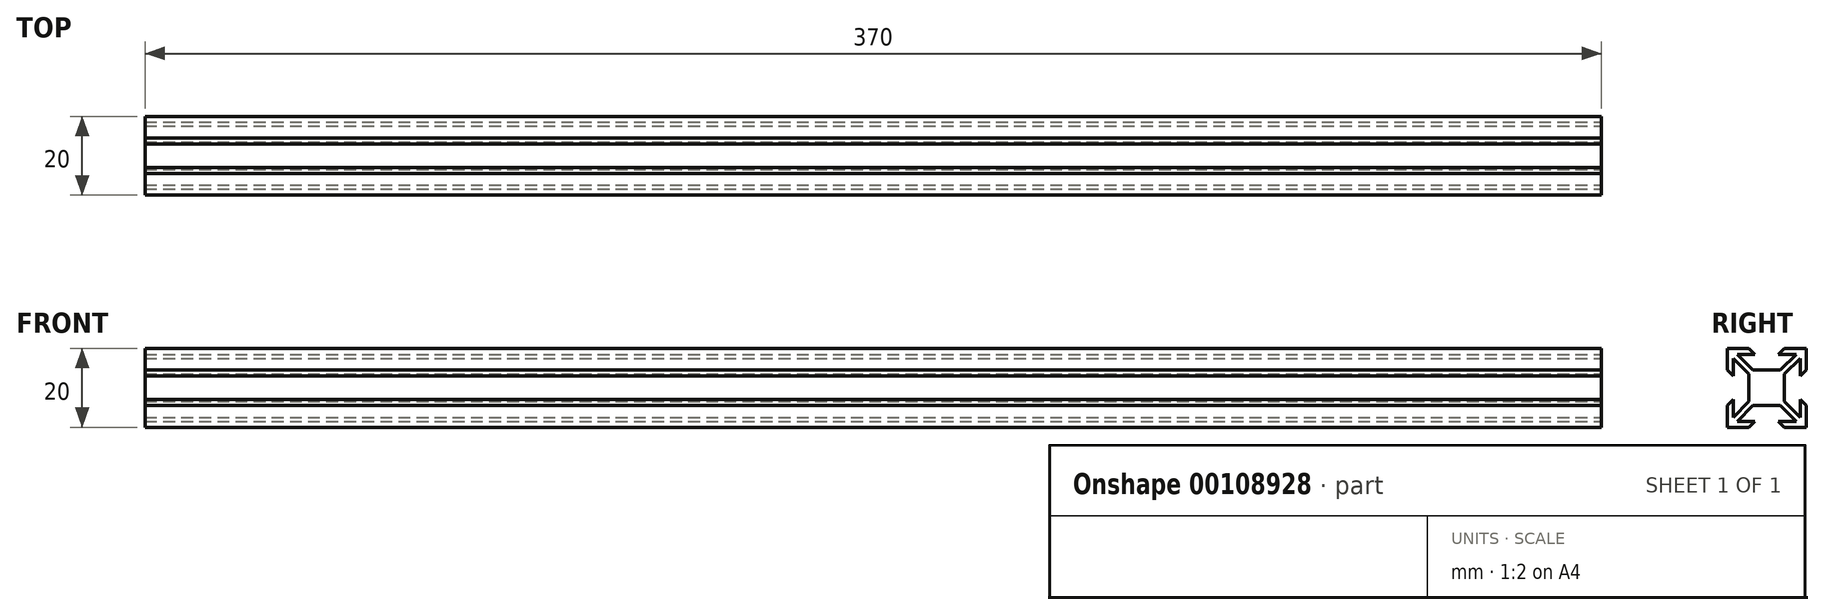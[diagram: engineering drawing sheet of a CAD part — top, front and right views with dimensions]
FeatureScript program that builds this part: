
annotation { "Feature Type Name" : "Feature", "Feature Type Description" : "" }
export const myFeature = defineFeature(function(context is Context, id is Id, definition is map)
    precondition{}
    {
        {
            var Q0;
            Q0=qCreatedBy(makeId("Top.planeOp"),FACE);
            var sketch = newSketch(context, id + "F0", { "sketchPlane" : qUnion([Q0])});
            skLineSegment(sketch, "E0.bottom", {"start": v(-185, 10) * mm, "end": v(185, 10) * mm});
            skLineSegment(sketch, "E0.top", {"start": v(-185, -10) * mm, "end": v(185, -10) * mm});
            skLineSegment(sketch, "E0.left", {"start": v(-185, 10) * mm, "end": v(-185, -10) * mm});
            skLineSegment(sketch, "E0.right", {"start": v(185, 10) * mm, "end": v(185, -10) * mm});
            skPoint(sketch, "E0.middle", {"position": v(0, 0) * mm});
            skSolve(sketch);
        }
        {
            var Q0;
            Q0=makeQuery(id+"F0.imprint","IMPRINT",FACE,{"disambiguationData":[TD([[makeQuery(id+"F0.imprint","IMPRINT",EDGE,{"derivedFrom":sQuery(id+"F0.wireOp",EDGE,"E0.bottom")}),-1.0]])]});
            extrude(context, id + "F1", {"entities" : qUnion([Q0]), "endBound" : BoundingType.SYMMETRIC, "depth" : 20 * mm});
        }
        {
            var Q0;
            Q0=makeQuery(id+"F1.opExtrude","SWEPT_FACE",FACE,{"disambiguationData":[OSD([sQuery(id+"F0.wireOp",EDGE,"E0.right")])]});
            var sketch = newSketch(context, id + "F2", { "sketchPlane" : qUnion([Q0])});
            skLineSegment(sketch, "E1", {"start": v(-4.5, 10) * mm, "end": v(-3, 8.5) * mm});
            skLineSegment(sketch, "E2", {"start": v(-3, 8.5) * mm, "end": v(-7.5, 8.5) * mm});
            skLineSegment(sketch, "E3", {"start": v(-7.5, 8.5) * mm, "end": v(-3.5, 4.5) * mm});
            skLineSegment(sketch, "E4", {"start": v(-3.5, 4.5) * mm, "end": v(0, 4.5) * mm});
            skLineSegment(sketch, "E5", {"start": v(0, 10) * mm, "end": v(0, -10) * mm, "construction": true});
            skLineSegment(sketch, "E6", {"start": v(-10, 0) * mm, "end": v(10, 0) * mm, "construction": true});
            skLineSegment(sketch, "E7.MirrorCS", {"start": v(-3.5, -4.5) * mm, "end": v(0, -4.5) * mm});
            skLineSegment(sketch, "E8.MirrorCS", {"start": v(-7.5, -8.5) * mm, "end": v(-3.5, -4.5) * mm});
            skLineSegment(sketch, "E9.MirrorCS", {"start": v(-3, -8.5) * mm, "end": v(-7.5, -8.5) * mm});
            skLineSegment(sketch, "E10.MirrorCS", {"start": v(-4.5, -10) * mm, "end": v(-3, -8.5) * mm});
            skLineSegment(sketch, "E11.MirrorCS", {"start": v(4.5, 10) * mm, "end": v(3, 8.5) * mm});
            skLineSegment(sketch, "E12.MirrorCS", {"start": v(3, 8.5) * mm, "end": v(7.5, 8.5) * mm});
            skLineSegment(sketch, "E13.MirrorCS", {"start": v(7.5, 8.5) * mm, "end": v(3.5, 4.5) * mm});
            skLineSegment(sketch, "E14.MirrorCS", {"start": v(3.5, 4.5) * mm, "end": v(0, 4.5) * mm});
            skLineSegment(sketch, "E15.MirrorCS", {"start": v(3.5, -4.5) * mm, "end": v(0, -4.5) * mm});
            skLineSegment(sketch, "E16.MirrorCS", {"start": v(7.5, -8.5) * mm, "end": v(3.5, -4.5) * mm});
            skLineSegment(sketch, "E17.MirrorCS", {"start": v(3, -8.5) * mm, "end": v(7.5, -8.5) * mm});
            skLineSegment(sketch, "E18.MirrorCS", {"start": v(4.5, -10) * mm, "end": v(3, -8.5) * mm});
            skLineSegment(sketch, "E19", {"start": v(-10, 4.5) * mm, "end": v(-8.5, 3) * mm});
            skLineSegment(sketch, "E20", {"start": v(-8.5, 3) * mm, "end": v(-8.5, 7.5) * mm});
            skLineSegment(sketch, "E21", {"start": v(-8.5, 7.5) * mm, "end": v(-4.5, 3.5) * mm});
            skLineSegment(sketch, "E22", {"start": v(-4.5, 3.5) * mm, "end": v(-4.5, 0) * mm});
            skLineSegment(sketch, "E23.MirrorCS", {"start": v(4.5, 3.5) * mm, "end": v(4.5, 0) * mm});
            skLineSegment(sketch, "E24.MirrorCS", {"start": v(8.5, 7.5) * mm, "end": v(4.5, 3.5) * mm});
            skLineSegment(sketch, "E25.MirrorCS", {"start": v(8.5, 3) * mm, "end": v(8.5, 7.5) * mm});
            skLineSegment(sketch, "E26.MirrorCS", {"start": v(10, 4.5) * mm, "end": v(8.5, 3) * mm});
            skLineSegment(sketch, "E27.MirrorCS", {"start": v(-4.5, -3.5) * mm, "end": v(-4.5, 0) * mm});
            skLineSegment(sketch, "E28.MirrorCS", {"start": v(-8.5, -7.5) * mm, "end": v(-4.5, -3.5) * mm});
            skLineSegment(sketch, "E29.MirrorCS", {"start": v(-8.5, -3) * mm, "end": v(-8.5, -7.5) * mm});
            skLineSegment(sketch, "E30.MirrorCS", {"start": v(-10, -4.5) * mm, "end": v(-8.5, -3) * mm});
            skLineSegment(sketch, "E31.MirrorCS", {"start": v(4.5, -3.5) * mm, "end": v(4.5, 0) * mm});
            skLineSegment(sketch, "E32.MirrorCS", {"start": v(8.5, -7.5) * mm, "end": v(4.5, -3.5) * mm});
            skLineSegment(sketch, "E33.MirrorCS", {"start": v(8.5, -3) * mm, "end": v(8.5, -7.5) * mm});
            skLineSegment(sketch, "E34.MirrorCS", {"start": v(10, -4.5) * mm, "end": v(8.5, -3) * mm});
            skSolve(sketch);
        }
        {
            var Q0;
            Q0 = qSketchRegion(id + "F2", true);
            var Q1;
            {var subQ0=sQuery(id+"F2.wireOp",EDGE,"E19");Q1=makeQuery(id+"F2.imprint","IMPRINT",FACE,{"disambiguationData":[TD([[makeQuery(id+"F2.imprint","IMPRINT",EDGE,{"derivedFrom":subQ0}),-1.0]])]});}
            var Q2;
            Q2=makeQuery(id+"F2.imprint","IMPRINT",FACE,{"disambiguationData":[TD([[makeQuery(id+"F2.imprint","IMPRINT",EDGE,{"derivedFrom":sQuery(id+"F2.wireOp",EDGE,"E7.MirrorCS")}),-1.0]])]});
            var Q3;
            Q3=makeQuery(id+"F2.imprint","IMPRINT",FACE,{"disambiguationData":[TD([[makeQuery(id+"F2.imprint","IMPRINT",EDGE,{"derivedFrom":sQuery(id+"F2.wireOp",EDGE,"E23.MirrorCS")}),1.0]])]});
            var Q4;
            {var subQ0=sQuery(id+"F2.wireOp",EDGE,"E1");Q4=makeQuery(id+"F2.imprint","IMPRINT",FACE,{"disambiguationData":[TD([[makeQuery(id+"F2.imprint","IMPRINT",EDGE,{"derivedFrom":subQ0}),1.0]])]});}
            extrude(context, id + "F3", {"entities" : qUnion([Q0, Q1, Q2, Q3, Q4]), "operationType" : NewBodyOperationType.REMOVE, "endBound" : BoundingType.THROUGH_ALL, "oppositeDirection" : true, "depth" : 25 * mm});
        }
    });
